# Revit family: Valve-Shower-KOHLER-MasterShower-K-2976_1
name_source: partatom
category: Plumbing Fixtures
revit_build: Autodesk Revit 2017 (Build: 20160225_1515(x64)
units: mm (PartAtom-declared; Revit-internal decimal feet)

## family parameters
Cut with Voids When Loaded = No
Host = Face
OmniClass Number = 23.31.17.00
OmniClass Title = Showers
Part Type = Normal
Room Calculation Point = No
Round Connector Dimension = Use Diameter
Shared = No

## types (1)
- NA - Brass
    ADA Compliant = No
    Assembly Code = D2010
    CW Connection = Yes
    Cold Water Inlet = Cold Water Inlet
    Date Modified = 11/23/2020
    Default Elevation = 42"
    Description = XVII 3/4 inch thermostatic valve with integral volume control and stops
    Drain Included = No
    Finish = Kohler-Metal-Brass
    Flow Rate = 17 GPM
    HW Connection = Yes
    Height = 6 15/16"
    Hot Water Inlet = Hot Water Inlet
    Length = 4 5/8"
    Manufacturer = KOHLER Co.
    MasterFormat 2014 = 22 41 39
    MasterFormat 2014 Name = Residential Faucets, Supplies, and Trim
    Material = Brass Construction
    Model = K-2976-KS-NA
    Pressure = 0.00 psi
    Product Documentation Link = https://www.us.kohler.com
    Product Name = MasterShower
    Product Page URL = http://www.us.kohler.com
    Tempered Water Outlet 1 = Tempered Water Outlet 1
    Tempered Water Outlet 2 = Tempered Water Outlet 2
    URL = https://www.us.kohler.com
    Vent Connection = No
    Waste Connection = No
    Waste Water Outlet = Waste Water Outlet
    Width = 4 13/16"

## geometry (parser evidence)
native form markers: Sweep x4
no freeform markers — native parametric forms only
